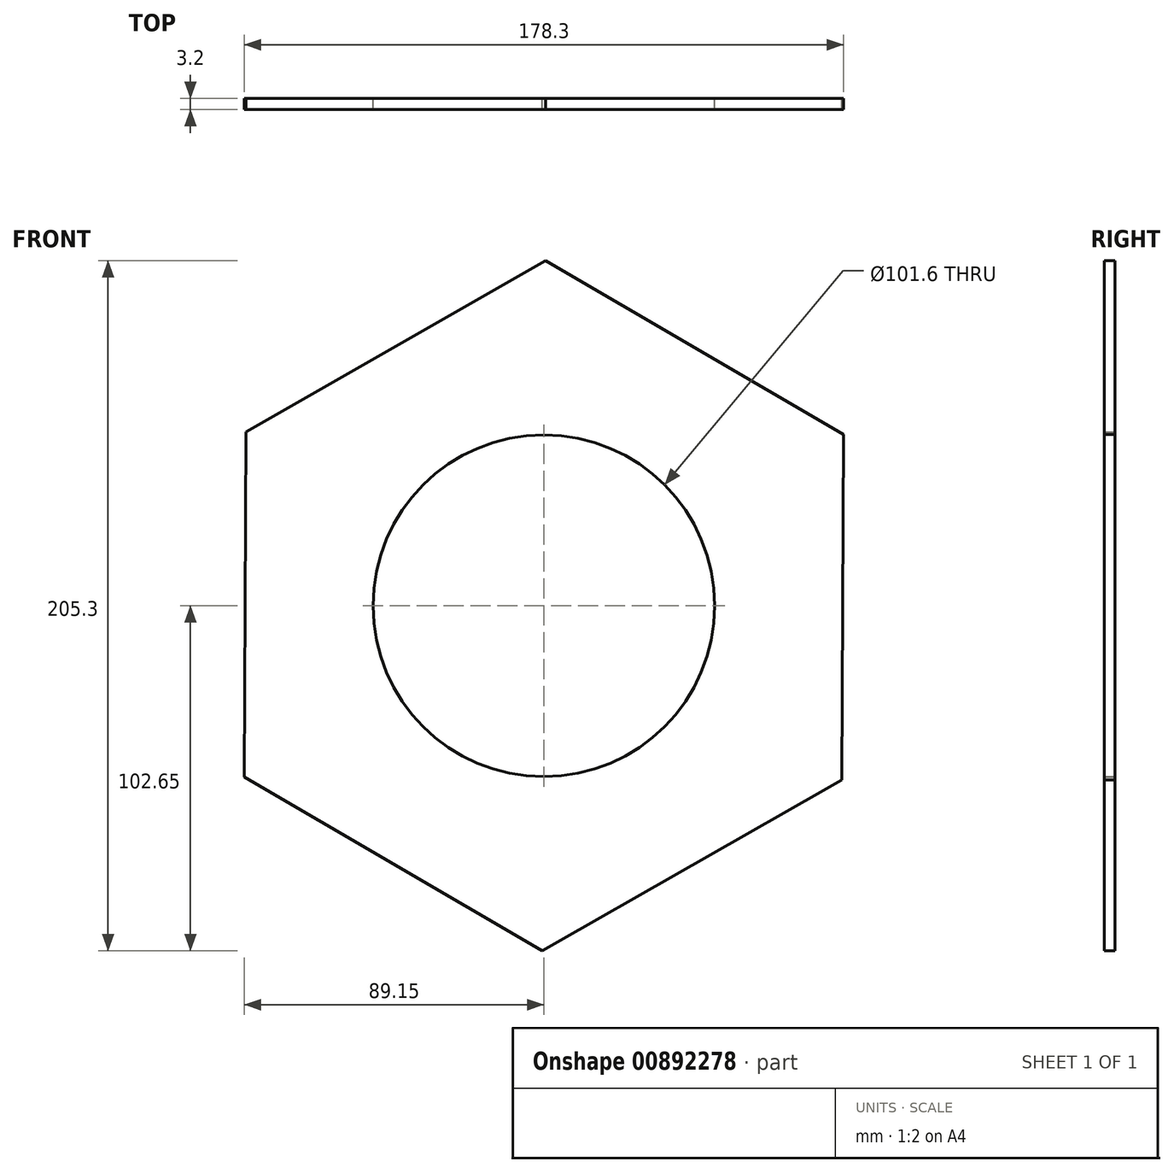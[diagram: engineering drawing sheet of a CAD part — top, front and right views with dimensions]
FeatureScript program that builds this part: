
annotation { "Feature Type Name" : "Feature", "Feature Type Description" : "" }
export const myFeature = defineFeature(function(context is Context, id is Id, definition is map)
    precondition{}
    {
        {
            var Q0;
            Q0=qCreatedBy(makeId("Front.planeOp"),FACE);
            var sketch = newSketch(context, id + "F0", { "sketchPlane" : qUnion([Q0])});
            skCircle(sketch, "E0.cCircle", {"center": v(0, 0) * mm, "radius": 88.9 * mm, "construction": true});
            skLineSegment(sketch, "E0.0", {"start": v(88.65, -51.75) * mm, "end": v(-0.5, -102.65) * mm});
            skLineSegment(sketch, "E0.1", {"start": v(-0.5, -102.65) * mm, "end": v(-89.15, -50.9) * mm});
            skLineSegment(sketch, "E0.2", {"start": v(-89.15, -50.9) * mm, "end": v(-88.65, 51.75) * mm});
            skLineSegment(sketch, "E0.3", {"start": v(-88.65, 51.75) * mm, "end": v(0.5, 102.65) * mm});
            skLineSegment(sketch, "E0.4", {"start": v(0.5, 102.65) * mm, "end": v(89.15, 50.9) * mm});
            skLineSegment(sketch, "E0.5", {"start": v(89.15, 50.9) * mm, "end": v(88.65, -51.75) * mm});
            skPoint(sketch, "E0.0.midPoint", {"position": v(44.08, -77.2) * mm});
            skCircle(sketch, "E1", {"center": v(0, 0) * mm, "radius": 50.8 * mm});
            skSolve(sketch);
        }
        {
            var Q0;
            Q0=makeQuery(id+"F0.imprint","IMPRINT",FACE,{"disambiguationData":[TD([[makeQuery(id+"F0.imprint","IMPRINT",EDGE,{"derivedFrom":sQuery(id+"F0.wireOp",EDGE,"E0.0")}),-1.0]])]});
            extrude(context, id + "F1", {"entities" : qUnion([Q0]), "depth" : 3.2 * mm, "offsetDistance" : 25.4 * mm});
        }
    });
